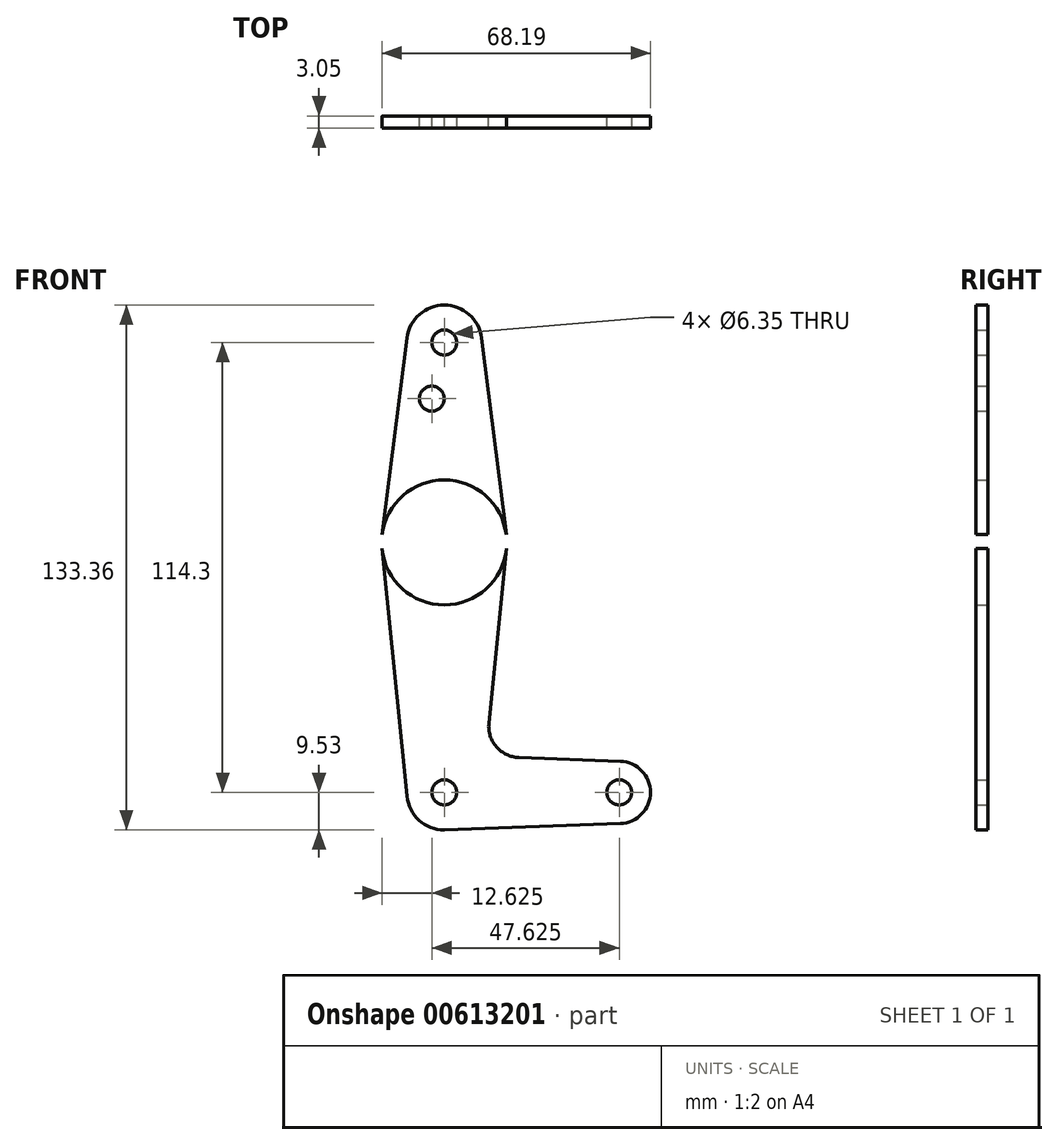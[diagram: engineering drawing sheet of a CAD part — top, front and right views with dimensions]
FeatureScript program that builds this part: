
annotation { "Feature Type Name" : "Feature", "Feature Type Description" : "" }
export const myFeature = defineFeature(function(context is Context, id is Id, definition is map)
    precondition{}
    {
        {
            var Q0;
            Q0=qCreatedBy(makeId("Front.planeOp"),FACE);
            var sketch = newSketch(context, id + "F0", { "sketchPlane" : qUnion([Q0])});
            skLineSegment(sketch, "E0", {"start": v(0, 114.3) * mm, "end": v(0, 0) * mm});
            skLineSegment(sketch, "E1", {"start": v(0, 0) * mm, "end": v(44.45, 0) * mm});
            skCircle(sketch, "E2", {"center": v(0, 114.3) * mm, "radius": 9.53 * mm});
            skCircle(sketch, "E3", {"center": v(0, 63.5) * mm, "radius": 15.88 * mm});
            skCircle(sketch, "E4", {"center": v(0, 0) * mm, "radius": 9.53 * mm});
            skCircle(sketch, "E5", {"center": v(44.45, 0) * mm, "radius": 7.94 * mm});
            skLineSegment(sketch, "E6", {"start": v(-9.45, 115.5) * mm, "end": v(-15.75, 65.48) * mm});
            skLineSegment(sketch, "E7", {"start": v(9.45, 115.5) * mm, "end": v(15.75, 65.48) * mm});
            skLineSegment(sketch, "E8", {"start": v(-9.48, -0.95) * mm, "end": v(-15.8, 61.91) * mm});
            skLineSegment(sketch, "E9", {"start": v(11.34, 17.6) * mm, "end": v(15.8, 61.91) * mm});
            skLineSegment(sketch, "E10", {"start": v(0, -9.53) * mm, "end": v(44.73, -7.93) * mm});
            skLineSegment(sketch, "E11", {"start": v(44.73, 7.93) * mm, "end": v(18.97, 8.85) * mm});
            skCircle(sketch, "E12", {"center": v(0, 114.3) * mm, "radius": 3.18 * mm});
            skCircle(sketch, "E13", {"center": v(0, 63.5) * mm, "radius": 3.18 * mm});
            skCircle(sketch, "E14", {"center": v(0, 0) * mm, "radius": 3.18 * mm});
            skCircle(sketch, "E15", {"center": v(44.45, 0) * mm, "radius": 3.18 * mm});
            skCircle(sketch, "E16", {"center": v(-3.17, 100.03) * mm, "radius": 3.18 * mm});
            skArc(sketch, "E17.filletArc", {"start": v(11.34, 17.6) * mm, "mid": v(13.26, 11.57) * mm, "end": v(18.97, 8.85) * mm});
            skSolve(sketch);
        }
        {
            var Q0;
            {var subQ0=sQuery(id+"F0.wireOp",EDGE,"E10");var subQ1=sQuery(id+"F0.wireOp",EDGE,"E4");var subQ2=makeQuery(id+"F0.imprint","INTERSECT",VERTEX,{"disambiguationData":[OD(0.0)],"derivedFrom":[subQ1,subQ0]});Q0=makeQuery(id+"F0.imprint","IMPRINT",FACE,{"disambiguationData":[TD([[makeQuery(id+"F0.imprint","IMPRINT",EDGE,{"disambiguationData":[TD([[subQ2,-1.0]])],"derivedFrom":subQ1}),1.0]])]});}
            var Q1;
            {var subQ0=sQuery(id+"F0.wireOp",EDGE,"E7");Q1=makeQuery(id+"F0.imprint","IMPRINT",FACE,{"disambiguationData":[TD([[makeQuery(id+"F0.imprint","IMPRINT",EDGE,{"derivedFrom":subQ0}),-1.0]])]});}
            var Q2;
            {var subQ5=sQuery(id+"F0.wireOp",EDGE,"E8");Q2=makeQuery(id+"F0.imprint","IMPRINT",FACE,{"disambiguationData":[TD([[makeQuery(id+"F0.imprint","IMPRINT",EDGE,{"derivedFrom":subQ5}),-1.0]])]});}
            var Q3;
            {var subQ0=sQuery(id+"F0.wireOp",EDGE,"E5");var subQ1=sQuery(id+"F0.wireOp",EDGE,"E1");var subQ2=makeQuery(id+"F0.imprint","INTERSECT",VERTEX,{"derivedFrom":[subQ1,subQ0]});Q3=makeQuery(id+"F0.imprint","IMPRINT",FACE,{"disambiguationData":[TD([[makeQuery(id+"F0.imprint","IMPRINT",EDGE,{"disambiguationData":[TD([[subQ2,1.0]])],"derivedFrom":subQ1}),-1.0]])]});}
            var Q4;
            Q4=makeQuery(id+"F0.imprint","IMPRINT",FACE,{"disambiguationData":[TD([[makeQuery(id+"F0.imprint","IMPRINT",EDGE,{"derivedFrom":sQuery(id+"F0.wireOp",EDGE,"E12")}),-1.0]])]});
            var Q5;
            Q5=makeQuery(id+"F0.imprint","IMPRINT",FACE,{"disambiguationData":[TD([[makeQuery(id+"F0.imprint","IMPRINT",EDGE,{"derivedFrom":sQuery(id+"F0.wireOp",EDGE,"E15")}),-1.0]])]});
            var Q6;
            {var subQ0=sQuery(id+"F0.wireOp",EDGE,"E6");Q6=makeQuery(id+"F0.imprint","IMPRINT",FACE,{"disambiguationData":[TD([[makeQuery(id+"F0.imprint","IMPRINT",EDGE,{"derivedFrom":subQ0}),1.0]])]});}
            var Q7;
            {var subQ0=sQuery(id+"F0.wireOp",EDGE,"E3");var subQ2=sQuery(id+"F0.wireOp",EDGE,"E0");var subQ5=makeQuery(id+"F0.imprint","INTERSECT",VERTEX,{"disambiguationData":[OD(0.0)],"derivedFrom":[subQ2,subQ0]});Q7=makeQuery(id+"F0.imprint","IMPRINT",FACE,{"disambiguationData":[TD([[makeQuery(id+"F0.imprint","IMPRINT",EDGE,{"disambiguationData":[TD([[subQ5,-1.0]])],"derivedFrom":subQ2}),1.0]])]});}
            var Q8;
            {var subQ0=sQuery(id+"F0.wireOp",EDGE,"E3");var subQ3=sQuery(id+"F0.wireOp",EDGE,"E0");var subQ4=makeQuery(id+"F0.imprint","INTERSECT",VERTEX,{"disambiguationData":[OD(0.0)],"derivedFrom":[subQ3,subQ0]});Q8=makeQuery(id+"F0.imprint","IMPRINT",FACE,{"disambiguationData":[TD([[makeQuery(id+"F0.imprint","IMPRINT",EDGE,{"disambiguationData":[TD([[subQ4,-1.0]])],"derivedFrom":subQ3}),-1.0]])]});}
            var Q9;
            {var subQ0=sQuery(id+"F0.wireOp",EDGE,"E4");var subQ8=sQuery(id+"F0.wireOp",EDGE,"E0");var subQ9=makeQuery(id+"F0.imprint","INTERSECT",VERTEX,{"derivedFrom":[subQ8,subQ0]});Q9=makeQuery(id+"F0.imprint","IMPRINT",FACE,{"disambiguationData":[TD([[makeQuery(id+"F0.imprint","IMPRINT",EDGE,{"disambiguationData":[TD([[subQ9,-1.0]])],"derivedFrom":subQ8}),-1.0]])]});}
            var Q10;
            {var subQ0=sQuery(id+"F0.wireOp",EDGE,"E4");var subQ1=sQuery(id+"F0.wireOp",EDGE,"E0");var subQ2=makeQuery(id+"F0.imprint","INTERSECT",VERTEX,{"derivedFrom":[subQ1,subQ0]});Q10=makeQuery(id+"F0.imprint","IMPRINT",FACE,{"disambiguationData":[TD([[makeQuery(id+"F0.imprint","IMPRINT",EDGE,{"disambiguationData":[TD([[subQ2,-1.0]])],"derivedFrom":subQ1}),1.0]])]});}
            var Q11;
            {var subQ0=sQuery(id+"F0.wireOp",EDGE,"E9");Q11=makeQuery(id+"F0.imprint","IMPRINT",FACE,{"disambiguationData":[TD([[makeQuery(id+"F0.imprint","IMPRINT",EDGE,{"derivedFrom":subQ0}),1.0]])]});}
            extrude(context, id + "F1", {"entities" : qUnion([Q0, Q1, Q2, Q3, Q4, Q5, Q6, Q7, Q8, Q9, Q10, Q11]), "depth" : 3.05 * mm, "offsetDistance" : 25.4 * mm});
        }
    });
